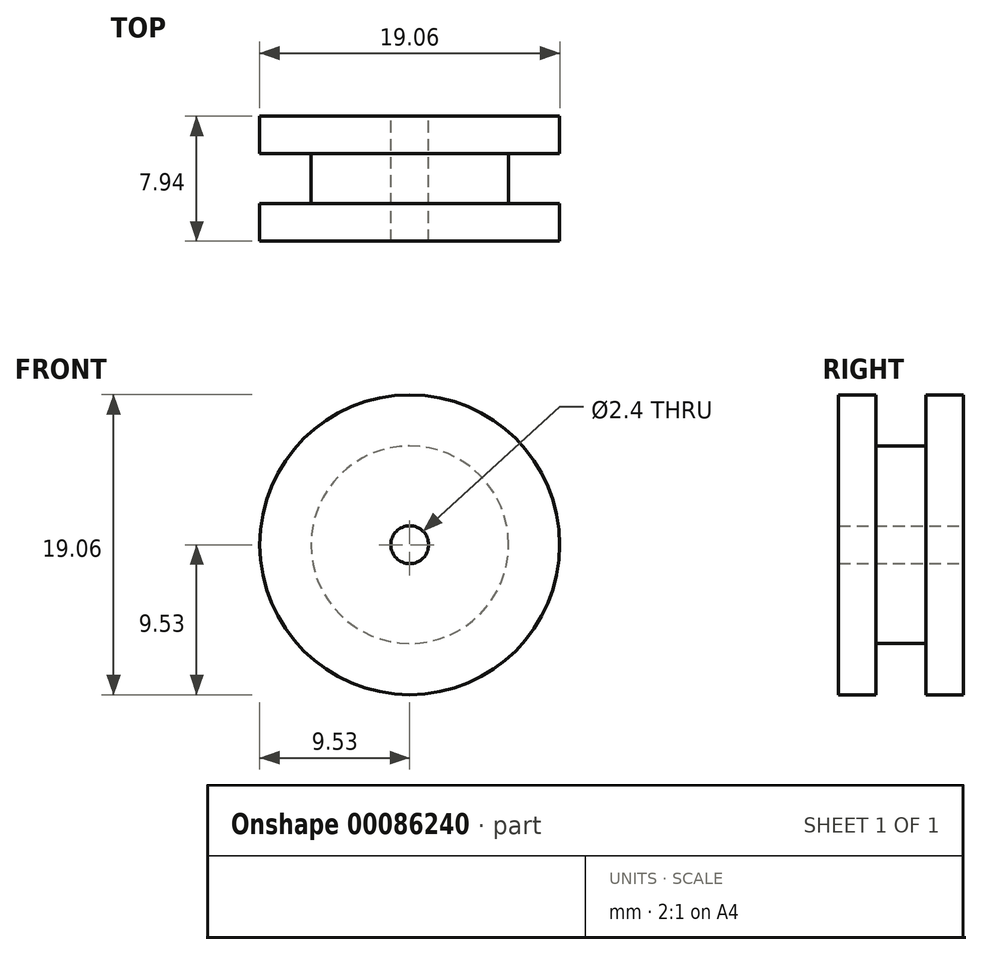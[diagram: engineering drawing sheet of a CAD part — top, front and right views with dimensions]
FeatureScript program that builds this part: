
annotation { "Feature Type Name" : "Feature", "Feature Type Description" : "" }
export const myFeature = defineFeature(function(context is Context, id is Id, definition is map)
    precondition{}
    {
        {
            var Q0;
            Q0=qCreatedBy(makeId("Right.planeOp"),FACE);
            var sketch = newSketch(context, id + "F0", { "sketchPlane" : qUnion([Q0])});
            skLineSegment(sketch, "E0", {"start": v(0, 0) * mm, "end": v(-3.97, 0) * mm});
            skLineSegment(sketch, "E1", {"start": v(-3.97, 0) * mm, "end": v(-3.97, 9.52) * mm});
            skLineSegment(sketch, "E2", {"start": v(-3.97, 9.52) * mm, "end": v(-1.59, 9.52) * mm});
            skLineSegment(sketch, "E3", {"start": v(-1.59, 9.52) * mm, "end": v(-1.59, 6.27) * mm});
            skLineSegment(sketch, "E4", {"start": v(-1.59, 6.27) * mm, "end": v(1.59, 6.27) * mm});
            skLineSegment(sketch, "E5", {"start": v(1.59, 6.27) * mm, "end": v(1.59, 9.52) * mm});
            skLineSegment(sketch, "E6", {"start": v(1.59, 9.52) * mm, "end": v(3.97, 9.52) * mm});
            skLineSegment(sketch, "E7", {"start": v(3.97, 9.53) * mm, "end": v(3.97, 0) * mm});
            skLineSegment(sketch, "E8", {"start": v(3.97, 0) * mm, "end": v(0, 0) * mm});
            skPoint(sketch, "E9", {"position": v(0, 6.27) * mm});
            skSolve(sketch);
        }
        {
            var Q0;
            Q0=makeQuery(id+"F0.imprint","IMPRINT",FACE,{"disambiguationData":[TD([[makeQuery(id+"F0.imprint","IMPRINT",EDGE,{"derivedFrom":sQuery(id+"F0.wireOp",EDGE,"E0")}),-1.0]])]});
            var Q1;
            Q1=sQuery(id+"F0.wireOp",EDGE,"E8");
            revolve(context, id + "F1", {"entities" : qUnion([Q0]), "axis" : qUnion([Q1]), "revolveType" : RevolveType.FULL});
        }
        {
            var Q0;
            Q0=makeQuery(id+"F1.opRevolve","SWEPT_FACE",FACE,{"disambiguationData":[OSD([sQuery(id+"F0.wireOp",EDGE,"E1")])]});
            var sketch = newSketch(context, id + "F2", { "sketchPlane" : qUnion([Q0])});
            skPoint(sketch, "E10", {"position": v(0, 0) * mm});
            skSolve(sketch);
        }
        {
            var Q0;
            Q0=sQuery(id+"F2.wireOp",VERTEX,"E10");
            var Q1;
            Q1=makeQuery(id+"F1.opRevolve","SWEPT_BODY",BODY,{"disambiguationData":[OSD([sQuery(id+"F0.wireOp",EDGE,"E0"),sQuery(id+"F0.wireOp",EDGE,"E1"),sQuery(id+"F0.wireOp",EDGE,"E2"),sQuery(id+"F0.wireOp",EDGE,"E3"),sQuery(id+"F0.wireOp",EDGE,"E4"),sQuery(id+"F0.wireOp",EDGE,"E5"),sQuery(id+"F0.wireOp",EDGE,"E6"),sQuery(id+"F0.wireOp",EDGE,"E7"),sQuery(id+"F0.wireOp",EDGE,"E8")])]});
            hole(context, id + "F3", {"style" : HoleStyle.SIMPLE, "endStyle" : HoleEndStyle.THROUGH, "standardTappedOrClearance" : lookupTablePath({ "standard" : "ISO", "engagement" : "75%", "pitch" : "0.6 mm", "size" : "M3", "type" : "Tapped" }), "standardBlindInLast" : lookupTablePath({ "standard" : "ISO", "engagement" : "75%", "pitch" : "0.6 mm", "size" : "M3", "type" : "Tapped" }), "holeDiameter" : 2.4 * mm, "locations" : qUnion([Q0]), "scope" : qUnion([Q1]), "isTappedThrough" : true, "showTappedDepth" : true});
        }
    });
